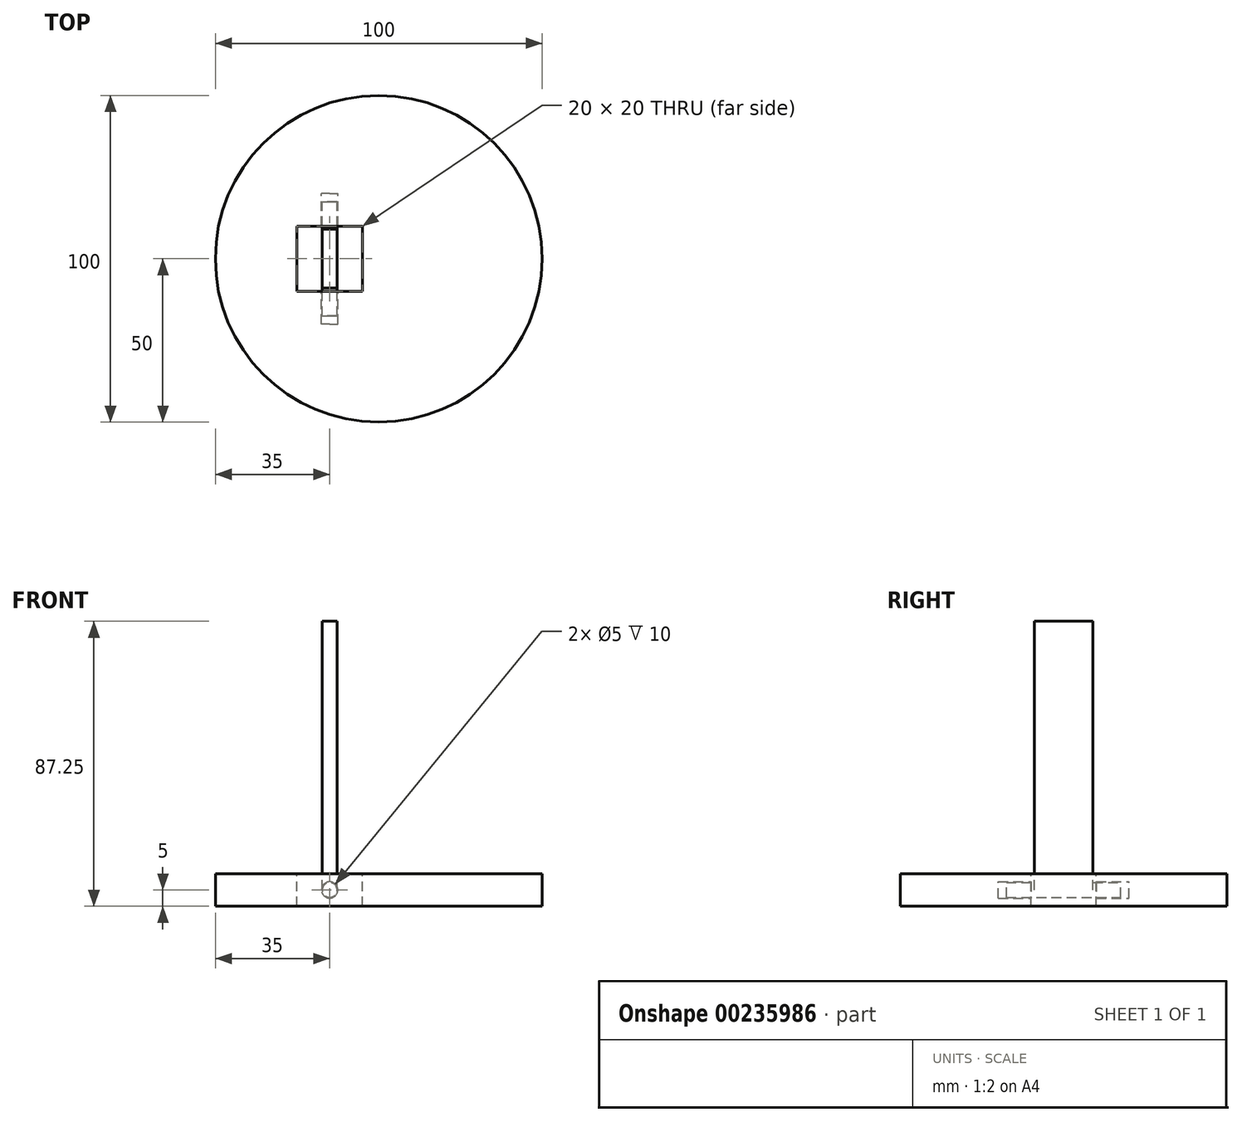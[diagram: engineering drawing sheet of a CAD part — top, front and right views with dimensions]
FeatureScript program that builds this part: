
annotation { "Feature Type Name" : "Feature", "Feature Type Description" : "" }
export const myFeature = defineFeature(function(context is Context, id is Id, definition is map)
    precondition{}
    {
        {
            var Q0;
            Q0=qCreatedBy(makeId("Top.planeOp"),FACE);
            var sketch = newSketch(context, id + "F0", { "sketchPlane" : qUnion([Q0])});
            skCircle(sketch, "E0", {"center": v(0, 0) * mm, "radius": 50 * mm});
            skSolve(sketch);
        }
        {
            var Q0;
            Q0 = qSketchRegion(id + "F0", true);
            extrude(context, id + "F1", {"entities" : qUnion([Q0]), "depth" : 10 * mm});
        }
        {
            var Q0;
            Q0=makeQuery(id+"F1.opExtrude","CAP_FACE",FACE,{"disambiguationData":[OSD([sQuery(id+"F0.wireOp",EDGE,"E0")])],"isStart":false});
            var sketch = newSketch(context, id + "F2", { "sketchPlane" : qUnion([Q0])});
            skLineSegment(sketch, "E1.bottom", {"start": v(-5, -10) * mm, "end": v(-25, -10) * mm});
            skLineSegment(sketch, "E1.top", {"start": v(-5, 10) * mm, "end": v(-25, 10) * mm});
            skLineSegment(sketch, "E1.left", {"start": v(-5, -10) * mm, "end": v(-5, 10) * mm});
            skLineSegment(sketch, "E1.right", {"start": v(-25, -10) * mm, "end": v(-25, 10) * mm});
            skPoint(sketch, "E1.middle", {"position": v(-15, 0) * mm});
            skSolve(sketch);
        }
        {
            var Q0;
            Q0=makeQuery(id+"F2.imprint","IMPRINT",FACE,{"disambiguationData":[TD([[makeQuery(id+"F2.imprint","IMPRINT",EDGE,{"derivedFrom":sQuery(id+"F2.wireOp",EDGE,"E1.bottom")}),-1.0]])]});
            extrude(context, id + "F3", {"entities" : qUnion([Q0]), "operationType" : NewBodyOperationType.REMOVE, "oppositeDirection" : true, "depth" : 25 * mm});
        }
        {
            var Q0;
            Q0=qCreatedBy(makeId("Front.planeOp"),FACE);
            var sketch = newSketch(context, id + "F4", { "sketchPlane" : qUnion([Q0])});
            skCircle(sketch, "E2", {"center": v(-15, 5) * mm, "radius": 2.5 * mm});
            skLineSegment(sketch, "E3.0.0", {"start": v(-5, 0) * mm, "end": v(-5, 10) * mm});
            skLineSegment(sketch, "E3.0.1", {"start": v(-5, 10) * mm, "end": v(-25, 10) * mm});
            skLineSegment(sketch, "E3.0.2", {"start": v(-25, 10) * mm, "end": v(-25, 0) * mm});
            skLineSegment(sketch, "E3.0.3", {"start": v(-25, 0) * mm, "end": v(-5, 0) * mm});
            skSolve(sketch);
        }
        {
            var Q0;
            Q0=makeQuery(id+"F4.imprint","IMPRINT",FACE,{"disambiguationData":[TD([[makeQuery(id+"F4.imprint","IMPRINT",EDGE,{"derivedFrom":sQuery(id+"F4.wireOp",EDGE,"E2")}),1.0]])]});
            extrude(context, id + "F5", {"entities" : qUnion([Q0]), "operationType" : NewBodyOperationType.REMOVE, "endBound" : BoundingType.SYMMETRIC, "depth" : 40 * mm});
        }
        {
            var Q0;
            Q0=qCreatedBy(makeId("Front.planeOp"),FACE);
            var sketch = newSketch(context, id + "F6", { "sketchPlane" : qUnion([Q0])});
            skCircle(sketch, "E4.0", {"center": v(-15, 5) * mm, "radius": 2.5 * mm});
            skCircle(sketch, "E5", {"center": v(-15, 5) * mm, "radius": 2.25 * mm});
            skSolve(sketch);
        }
        {
            var Q0;
            Q0=makeQuery(id+"F6.imprint","IMPRINT",FACE,{"disambiguationData":[TD([[makeQuery(id+"F6.imprint","IMPRINT",EDGE,{"derivedFrom":sQuery(id+"F6.wireOp",EDGE,"E5")}),1.0]])]});
            extrude(context, id + "F7", {"entities" : qUnion([Q0]), "endBound" : BoundingType.SYMMETRIC, "depth" : 35 * mm});
        }
        {
            var Q0;
            Q0=qCreatedBy(makeId("Front.planeOp"),FACE);
            var sketch = newSketch(context, id + "F8", { "sketchPlane" : qUnion([Q0])});
            skLineSegment(sketch, "E6.top", {"start": v(-17.25, 87.25) * mm, "end": v(-12.75, 87.25) * mm});
            skLineSegment(sketch, "E6.left", {"start": v(-17.25, 5) * mm, "end": v(-17.25, 87.25) * mm});
            skLineSegment(sketch, "E6.right", {"start": v(-12.75, 5) * mm, "end": v(-12.75, 87.25) * mm});
            skArc(sketch, "E7", {"start": v(-17.25, 5) * mm, "mid": v(-15, 2.75) * mm, "end": v(-12.75, 5) * mm});
            skSolve(sketch);
        }
        {
            var Q0;
            Q0=makeQuery(id+"F8.imprint","IMPRINT",FACE,{"disambiguationData":[TD([[makeQuery(id+"F8.imprint","IMPRINT",EDGE,{"derivedFrom":sQuery(id+"F8.wireOp",EDGE,"E6.top")}),-1.0]])]});
            extrude(context, id + "F9", {"entities" : qUnion([Q0]), "operationType" : NewBodyOperationType.ADD, "endBound" : BoundingType.SYMMETRIC, "depth" : 18 * mm});
        }
    });
